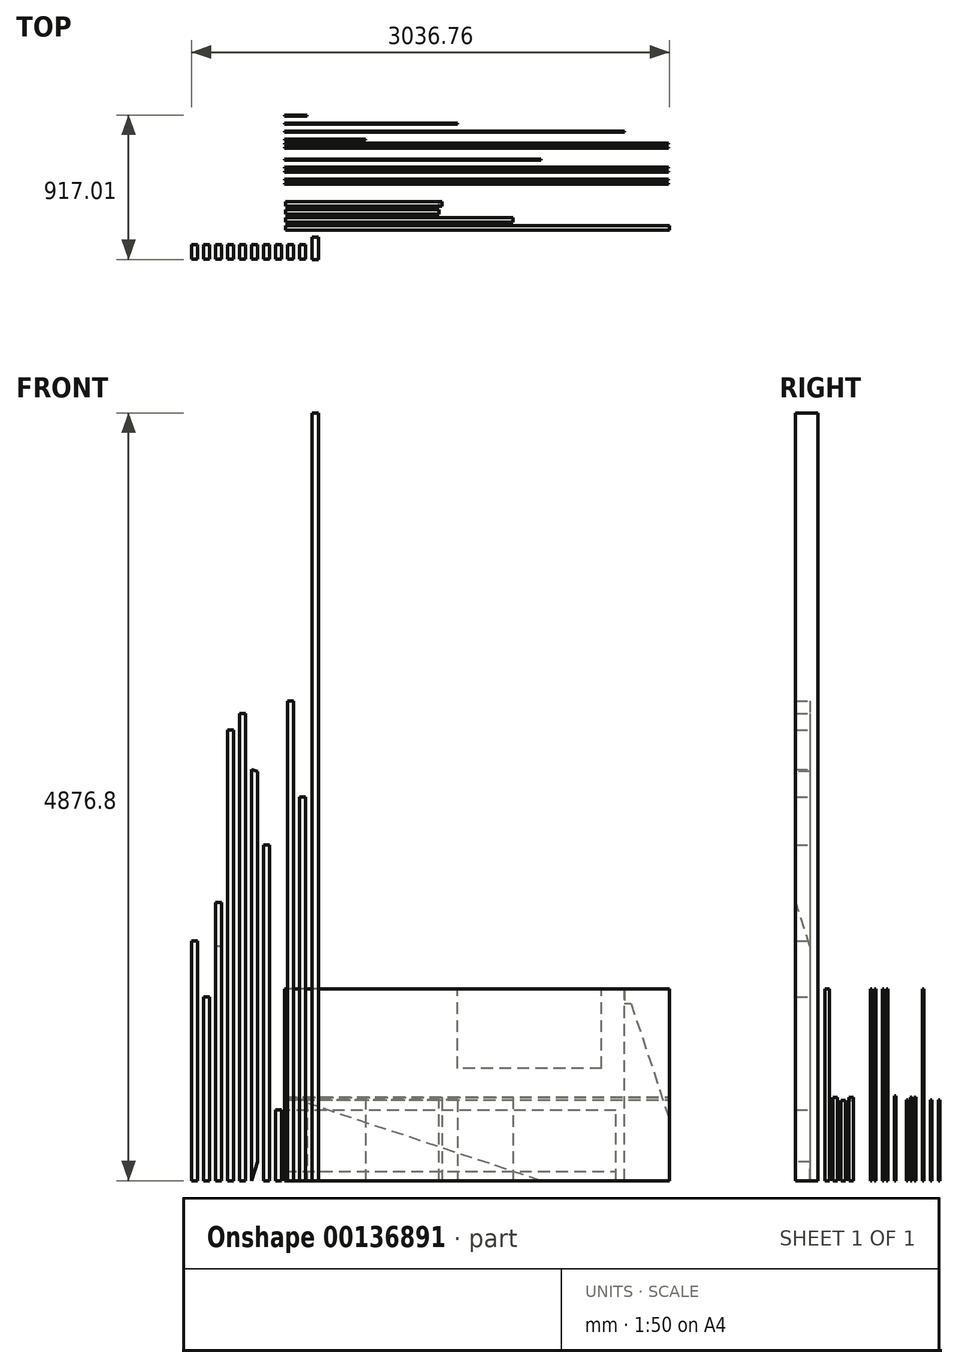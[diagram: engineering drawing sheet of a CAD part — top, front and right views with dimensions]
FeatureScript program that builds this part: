
annotation { "Feature Type Name" : "Feature", "Feature Type Description" : "" }
export const myFeature = defineFeature(function(context is Context, id is Id, definition is map)
    precondition{}
    {
        {
            var Q0;
            Q0=qCreatedBy(makeId("Top.planeOp"),FACE);
            var sketch = newSketch(context, id + "F0", { "sketchPlane" : qUnion([Q0])});
            skLineSegment(sketch, "E0.bottom", {"start": v(12.85, 155.38) * mm, "end": v(52.54, 155.38) * mm});
            skLineSegment(sketch, "E0.top", {"start": v(12.85, 12.5) * mm, "end": v(52.54, 12.5) * mm});
            skLineSegment(sketch, "E0.left", {"start": v(12.85, 155.38) * mm, "end": v(12.85, 12.5) * mm});
            skLineSegment(sketch, "E0.right", {"start": v(52.54, 155.38) * mm, "end": v(52.54, 12.5) * mm});
            skSolve(sketch);
        }
        {
            var Q0;
            Q0=makeQuery(id+"F0.imprint","IMPRINT",FACE,{"disambiguationData":[TD([[makeQuery(id+"F0.imprint","IMPRINT",EDGE,{"derivedFrom":sQuery(id+"F0.wireOp",EDGE,"E0.bottom")}),-1.0]])]});
            extrude(context, id + "F1", {"entities" : qUnion([Q0]), "depth" : 4876.8 * mm});
        }
        {
            var Q0;
            Q0=qCreatedBy(makeId("Top.planeOp"),FACE);
            var sketch = newSketch(context, id + "F2", { "sketchPlane" : qUnion([Q0])});
            skLineSegment(sketch, "E1.bottom", {"start": v(-27.7, 13.32) * mm, "end": v(-67.4, 13.32) * mm});
            skLineSegment(sketch, "E1.top", {"start": v(-27.7, 105.4) * mm, "end": v(-67.4, 105.4) * mm});
            skLineSegment(sketch, "E1.left", {"start": v(-27.7, 13.32) * mm, "end": v(-27.7, 105.4) * mm});
            skLineSegment(sketch, "E1.right", {"start": v(-67.4, 13.32) * mm, "end": v(-67.4, 105.4) * mm});
            skSolve(sketch);
        }
        {
            var Q0;
            Q0=makeQuery(id+"F2.imprint","IMPRINT",FACE,{"disambiguationData":[TD([[makeQuery(id+"F2.imprint","IMPRINT",EDGE,{"derivedFrom":sQuery(id+"F2.wireOp",EDGE,"E1.bottom")}),-1.0]])]});
            extrude(context, id + "F3", {"entities" : qUnion([Q0]), "depth" : 2438.4 * mm});
        }
        {
            var Q0;
            Q0=makeQuery(id+"F3.opExtrude","SWEPT_BODY",BODY,{"disambiguationData":[OSD([sQuery(id+"F2.wireOp",EDGE,"E1.bottom"),sQuery(id+"F2.wireOp",EDGE,"E1.top"),sQuery(id+"F2.wireOp",EDGE,"E1.left"),sQuery(id+"F2.wireOp",EDGE,"E1.right")])]});
            transform(context, id + "F4", {"entities" : qUnion([Q0]), "transformType" : TransformType.TRANSLATION_3D, "dx" : -76.2 * mm, "dy" : 0 * mm, "dz" : 0 * mm, "makeCopy" : true});
        }
        {
            var Q0;
            Q0=makeQuery(id+"F4.opPattern","COPY",FACE,{"derivedFrom":makeQuery(id+"F3.opExtrude","CAP_FACE",FACE,{"disambiguationData":[OSD([sQuery(id+"F2.wireOp",EDGE,"E1.bottom"),sQuery(id+"F2.wireOp",EDGE,"E1.top"),sQuery(id+"F2.wireOp",EDGE,"E1.left"),sQuery(id+"F2.wireOp",EDGE,"E1.right")])],"isStart":false}),"instanceName":"1"});
            extrude(context, id + "F5", {"entities" : qUnion([Q0]), "operationType" : NewBodyOperationType.ADD, "depth" : 609.6 * mm});
        }
        {
            var Q0;
            Q0=qCreatedBy(makeId("Top.planeOp"),FACE);
            var sketch = newSketch(context, id + "F6", { "sketchPlane" : qUnion([Q0])});
            skLineSegment(sketch, "E2.bottom", {"start": v(2283.56, 226) * mm, "end": v(-154.84, 226) * mm});
            skLineSegment(sketch, "E2.top", {"start": v(2283.56, 198.29) * mm, "end": v(-154.84, 198.29) * mm});
            skLineSegment(sketch, "E2.left", {"start": v(2283.56, 226) * mm, "end": v(2283.56, 198.29) * mm});
            skLineSegment(sketch, "E2.right", {"start": v(-154.84, 226) * mm, "end": v(-154.84, 198.29) * mm});
            skSolve(sketch);
        }
        {
            var Q0;
            Q0=makeQuery(id+"F6.imprint","IMPRINT",FACE,{"disambiguationData":[TD([[makeQuery(id+"F6.imprint","IMPRINT",EDGE,{"derivedFrom":sQuery(id+"F6.wireOp",EDGE,"E2.bottom")}),1.0]])]});
            extrude(context, id + "F7", {"entities" : qUnion([Q0]), "depth" : 1219.2 * mm});
        }
        {
            var Q0;
            Q0=makeQuery(id+"F3.opExtrude","SWEPT_BODY",BODY,{"disambiguationData":[OSD([sQuery(id+"F2.wireOp",EDGE,"E1.bottom"),sQuery(id+"F2.wireOp",EDGE,"E1.top"),sQuery(id+"F2.wireOp",EDGE,"E1.left"),sQuery(id+"F2.wireOp",EDGE,"E1.right")])]});
            transform(context, id + "F8", {"entities" : qUnion([Q0]), "transformType" : TransformType.TRANSLATION_3D, "dx" : -152.4 * mm, "dy" : 0 * mm, "dz" : 0 * mm, "makeCopy" : true});
        }
        {
            var Q0;
            Q0=makeQuery(id+"F8.opPattern","COPY",FACE,{"derivedFrom":makeQuery(id+"F3.opExtrude","CAP_FACE",FACE,{"disambiguationData":[OSD([sQuery(id+"F2.wireOp",EDGE,"E1.bottom"),sQuery(id+"F2.wireOp",EDGE,"E1.top"),sQuery(id+"F2.wireOp",EDGE,"E1.left"),sQuery(id+"F2.wireOp",EDGE,"E1.right")])],"isStart":false}),"instanceName":"1"});
            extrude(context, id + "F9", {"entities" : qUnion([Q0]), "operationType" : NewBodyOperationType.REMOVE, "oppositeDirection" : true, "depth" : 1987.55 * mm});
        }
        {
            var Q0;
            Q0=qCreatedBy(makeId("Top.planeOp"),FACE);
            var sketch = newSketch(context, id + "F10", { "sketchPlane" : qUnion([Q0])});
            skLineSegment(sketch, "E3.bottom", {"start": v(-155.66, 249.92) * mm, "end": v(1288.96, 249.92) * mm});
            skLineSegment(sketch, "E3.top", {"start": v(-155.66, 277.63) * mm, "end": v(1288.96, 277.63) * mm});
            skLineSegment(sketch, "E3.left", {"start": v(-155.66, 249.92) * mm, "end": v(-155.66, 277.63) * mm});
            skLineSegment(sketch, "E3.right", {"start": v(1288.96, 249.92) * mm, "end": v(1288.96, 277.63) * mm});
            skSolve(sketch);
        }
        {
            var Q0;
            Q0=makeQuery(id+"F10.imprint","IMPRINT",FACE,{"disambiguationData":[TD([[makeQuery(id+"F10.imprint","IMPRINT",EDGE,{"derivedFrom":sQuery(id+"F10.wireOp",EDGE,"E3.bottom")}),1.0]])]});
            extrude(context, id + "F11", {"entities" : qUnion([Q0]), "depth" : 530.23 * mm});
        }
        {
            var Q0;
            Q0=makeQuery(id+"F11.opExtrude","SWEPT_BODY",BODY,{"disambiguationData":[OSD([sQuery(id+"F10.wireOp",EDGE,"E3.bottom"),sQuery(id+"F10.wireOp",EDGE,"E3.top"),sQuery(id+"F10.wireOp",EDGE,"E3.left"),sQuery(id+"F10.wireOp",EDGE,"E3.right")])]});
            transform(context, id + "F12", {"entities" : qUnion([Q0]), "transformType" : TransformType.TRANSLATION_3D, "dx" : 0 * mm, "dy" : 50.8 * mm, "dz" : 0 * mm, "makeCopy" : true});
        }
        {
            var Q0;
            Q0=makeQuery(id+"F12.opPattern","COPY",FACE,{"derivedFrom":makeQuery(id+"F11.opExtrude","SWEPT_FACE",FACE,{"disambiguationData":[OSD([sQuery(id+"F10.wireOp",EDGE,"E3.right")])]}),"instanceName":"1"});
            extrude(context, id + "F13", {"entities" : qUnion([Q0]), "operationType" : NewBodyOperationType.REMOVE, "oppositeDirection" : true, "depth" : 450.85 * mm});
        }
        {
            var Q0;
            Q0=makeQuery(id+"F3.opExtrude","SWEPT_BODY",BODY,{"disambiguationData":[OSD([sQuery(id+"F2.wireOp",EDGE,"E1.bottom"),sQuery(id+"F2.wireOp",EDGE,"E1.top"),sQuery(id+"F2.wireOp",EDGE,"E1.left"),sQuery(id+"F2.wireOp",EDGE,"E1.right")])]});
            transform(context, id + "F14", {"entities" : qUnion([Q0]), "transformType" : TransformType.TRANSLATION_3D, "dx" : -228.6 * mm, "dy" : 0 * mm, "dz" : 0 * mm, "makeCopy" : true});
        }
        {
            var Q0;
            Q0=makeQuery(id+"F14.opPattern","COPY",FACE,{"derivedFrom":makeQuery(id+"F3.opExtrude","CAP_FACE",FACE,{"disambiguationData":[OSD([sQuery(id+"F2.wireOp",EDGE,"E1.bottom"),sQuery(id+"F2.wireOp",EDGE,"E1.top"),sQuery(id+"F2.wireOp",EDGE,"E1.left"),sQuery(id+"F2.wireOp",EDGE,"E1.right")])],"isStart":false}),"instanceName":"1"});
            extrude(context, id + "F15", {"entities" : qUnion([Q0]), "operationType" : NewBodyOperationType.REMOVE, "oppositeDirection" : true, "depth" : 304.8 * mm});
        }
        {
            var Q0;
            Q0=makeQuery(id+"F3.opExtrude","SWEPT_BODY",BODY,{"disambiguationData":[OSD([sQuery(id+"F2.wireOp",EDGE,"E1.bottom"),sQuery(id+"F2.wireOp",EDGE,"E1.top"),sQuery(id+"F2.wireOp",EDGE,"E1.left"),sQuery(id+"F2.wireOp",EDGE,"E1.right")])]});
            transform(context, id + "F16", {"entities" : qUnion([Q0]), "transformType" : TransformType.TRANSLATION_3D, "dx" : -457.2 * mm, "dy" : 0 * mm, "dz" : 0 * mm, "makeCopy" : true});
        }
        {
            var Q0;
            Q0=makeQuery(id+"F16.opPattern","COPY",FACE,{"derivedFrom":makeQuery(id+"F3.opExtrude","CAP_FACE",FACE,{"disambiguationData":[OSD([sQuery(id+"F2.wireOp",EDGE,"E1.bottom"),sQuery(id+"F2.wireOp",EDGE,"E1.top"),sQuery(id+"F2.wireOp",EDGE,"E1.left"),sQuery(id+"F2.wireOp",EDGE,"E1.right")])],"isStart":false}),"instanceName":"1"});
            extrude(context, id + "F17", {"entities" : qUnion([Q0]), "operationType" : NewBodyOperationType.ADD, "depth" : 425.45 * mm});
        }
        {
            var Q0;
            Q0=makeQuery(id+"F3.opExtrude","SWEPT_BODY",BODY,{"disambiguationData":[OSD([sQuery(id+"F2.wireOp",EDGE,"E1.bottom"),sQuery(id+"F2.wireOp",EDGE,"E1.top"),sQuery(id+"F2.wireOp",EDGE,"E1.left"),sQuery(id+"F2.wireOp",EDGE,"E1.right")])]});
            transform(context, id + "F18", {"entities" : qUnion([Q0]), "transformType" : TransformType.TRANSLATION_3D, "dx" : -304.8 * mm, "dy" : 0 * mm, "dz" : 0 * mm, "makeCopy" : true});
        }
        {
            var Q0;
            Q0=makeQuery(id+"F18.opPattern","COPY",FACE,{"derivedFrom":makeQuery(id+"F3.opExtrude","CAP_FACE",FACE,{"disambiguationData":[OSD([sQuery(id+"F2.wireOp",EDGE,"E1.bottom"),sQuery(id+"F2.wireOp",EDGE,"E1.top"),sQuery(id+"F2.wireOp",EDGE,"E1.left"),sQuery(id+"F2.wireOp",EDGE,"E1.right")])],"isStart":false}),"instanceName":"1"});
            extrude(context, id + "F19", {"entities" : qUnion([Q0]), "operationType" : NewBodyOperationType.ADD, "depth" : 172.56 * mm});
        }
        {
            var Q0;
            {var subQ0=sQuery(id+"F2.wireOp",EDGE,"E1.bottom");Q0=makeQuery(id+"F19.boolean.opBoolean","MERGE",FACE,{"derivedFrom":[makeQuery(id+"F18.opPattern","COPY",FACE,{"derivedFrom":makeQuery(id+"F3.opExtrude","SWEPT_FACE",FACE,{"disambiguationData":[OSD([subQ0])]}),"instanceName":"1"}),makeQuery(id+"F19.opExtrude","SWEPT_FACE",FACE,{"disambiguationData":[OSD([subQ0])]})]});}
            var sketch = newSketch(context, id + "F20", { "sketchPlane" : qUnion([Q0])});
            skLineSegment(sketch, "E4", {"start": v(-372.2, 2610.96) * mm, "end": v(-332.5, 2597.8) * mm});
            skLineSegment(sketch, "E5", {"start": v(-372.2, 0) * mm, "end": v(-332.5, 119.6) * mm});
            skSolve(sketch);
        }
        {
            var Q0;
            {var subQ0=sQuery(id+"F20.wireOp",EDGE,"E5");Q0=makeQuery(id+"F20.imprint","IMPRINT",FACE,{"disambiguationData":[TD([[makeQuery(id+"F20.imprint","IMPRINT",EDGE,{"derivedFrom":subQ0}),-1.0]])]});}
            var Q1;
            {var subQ0=sQuery(id+"F20.wireOp",EDGE,"E4");Q1=makeQuery(id+"F20.imprint","IMPRINT",FACE,{"disambiguationData":[TD([[makeQuery(id+"F20.imprint","IMPRINT",EDGE,{"derivedFrom":subQ0}),1.0]])]});}
            extrude(context, id + "F21", {"entities" : qUnion([Q0, Q1]), "operationType" : NewBodyOperationType.REMOVE, "oppositeDirection" : true, "depth" : 152.4 * mm});
        }
        {
            var Q0;
            Q0=makeQuery(id+"F3.opExtrude","SWEPT_BODY",BODY,{"disambiguationData":[OSD([sQuery(id+"F2.wireOp",EDGE,"E1.bottom"),sQuery(id+"F2.wireOp",EDGE,"E1.top"),sQuery(id+"F2.wireOp",EDGE,"E1.left"),sQuery(id+"F2.wireOp",EDGE,"E1.right")])]});
            transform(context, id + "F22", {"entities" : qUnion([Q0]), "transformType" : TransformType.TRANSLATION_3D, "dx" : -381 * mm, "dy" : 0 * mm, "dz" : 0 * mm, "makeCopy" : true});
        }
        {
            var Q0;
            Q0=makeQuery(id+"F22.opPattern","COPY",FACE,{"derivedFrom":makeQuery(id+"F3.opExtrude","CAP_FACE",FACE,{"disambiguationData":[OSD([sQuery(id+"F2.wireOp",EDGE,"E1.bottom"),sQuery(id+"F2.wireOp",EDGE,"E1.top"),sQuery(id+"F2.wireOp",EDGE,"E1.left"),sQuery(id+"F2.wireOp",EDGE,"E1.right")])],"isStart":false}),"instanceName":"1"});
            extrude(context, id + "F23", {"entities" : qUnion([Q0]), "operationType" : NewBodyOperationType.ADD, "depth" : 530.23 * mm});
        }
        {
            var Q0;
            Q0=qCreatedBy(makeId("Top.planeOp"),FACE);
            var sketch = newSketch(context, id + "F24", { "sketchPlane" : qUnion([Q0])});
            skLineSegment(sketch, "E6.bottom", {"start": v(-162.06, 488.98) * mm, "end": v(2276.34, 488.98) * mm});
            skLineSegment(sketch, "E6.top", {"start": v(-162.06, 497.72) * mm, "end": v(2276.34, 497.72) * mm});
            skLineSegment(sketch, "E6.left", {"start": v(-162.06, 488.98) * mm, "end": v(-162.06, 497.72) * mm});
            skLineSegment(sketch, "E6.right", {"start": v(2276.34, 488.98) * mm, "end": v(2276.34, 497.72) * mm});
            skSolve(sketch);
        }
        {
            var Q0;
            Q0=makeQuery(id+"F24.imprint","IMPRINT",FACE,{"disambiguationData":[TD([[makeQuery(id+"F24.imprint","IMPRINT",EDGE,{"derivedFrom":sQuery(id+"F24.wireOp",EDGE,"E6.bottom")}),1.0]])]});
            extrude(context, id + "F25", {"entities" : qUnion([Q0]), "depth" : 1219.2 * mm});
        }
        {
            var Q0;
            Q0=makeQuery(id+"F12.opPattern","COPY",FACE,{"derivedFrom":makeQuery(id+"F11.opExtrude","SWEPT_FACE",FACE,{"disambiguationData":[OSD([sQuery(id+"F10.wireOp",EDGE,"E3.top")])]}),"instanceName":"1"});
            var sketch = newSketch(context, id + "F26", { "sketchPlane" : qUnion([Q0])});
            skLineSegment(sketch, "E7", {"start": v(-818.27, 0) * mm, "end": v(-818.27, 510.38) * mm});
            skLineSegment(sketch, "E8", {"start": v(-818.27, 510.38) * mm, "end": v(155.66, 510.38) * mm});
            skSolve(sketch);
        }
        {
            var Q0;
            Q0=makeQuery(id+"F12.opPattern","COPY",BODY,{"derivedFrom":makeQuery(id+"F11.opExtrude","SWEPT_BODY",BODY,{"disambiguationData":[OSD([sQuery(id+"F10.wireOp",EDGE,"E3.bottom"),sQuery(id+"F10.wireOp",EDGE,"E3.top"),sQuery(id+"F10.wireOp",EDGE,"E3.left"),sQuery(id+"F10.wireOp",EDGE,"E3.right")])]}),"instanceName":"1"});
            transform(context, id + "F27", {"entities" : qUnion([Q0]), "transformType" : TransformType.TRANSLATION_3D, "dx" : 0 * mm, "dy" : 50.8 * mm, "dz" : 0 * mm, "makeCopy" : true});
        }
        {
            var Q0;
            Q0=makeQuery(id+"F27.opPattern","COPY",FACE,{"derivedFrom":makeQuery(id+"F12.opPattern","COPY",FACE,{"derivedFrom":makeQuery(id+"F11.opExtrude","SWEPT_FACE",FACE,{"disambiguationData":[OSD([sQuery(id+"F10.wireOp",EDGE,"E3.top")])]}),"instanceName":"1"}),"instanceName":"1"});
            var sketch = newSketch(context, id + "F28", { "sketchPlane" : qUnion([Q0])});
            skLineSegment(sketch, "E9", {"start": v(-818.27, 0) * mm, "end": v(-818.27, 510.38) * mm});
            skLineSegment(sketch, "E10", {"start": v(-818.27, 510.38) * mm, "end": v(155.66, 510.38) * mm});
            skSolve(sketch);
        }
        {
            var Q0;
            {var subQ4=sQuery(id+"F26.wireOp",EDGE,"E7");Q0=makeQuery(id+"F26.imprint","IMPRINT",FACE,{"disambiguationData":[TD([[makeQuery(id+"F26.imprint","IMPRINT",EDGE,{"derivedFrom":subQ4}),1.0]])]});}
            extrude(context, id + "F29", {"entities" : qUnion([Q0]), "operationType" : NewBodyOperationType.REMOVE, "oppositeDirection" : true, "depth" : 50.8 * mm});
        }
        {
            var Q0;
            {var subQ0=sQuery(id+"F28.wireOp",EDGE,"E9");Q0=makeQuery(id+"F28.imprint","IMPRINT",FACE,{"disambiguationData":[TD([[makeQuery(id+"F28.imprint","IMPRINT",EDGE,{"derivedFrom":subQ0}),-1.0]])]});}
            extrude(context, id + "F30", {"entities" : qUnion([Q0]), "operationType" : NewBodyOperationType.REMOVE, "oppositeDirection" : true, "depth" : 50.8 * mm});
        }
        {
            var Q0;
            Q0=makeQuery(id+"F25.opExtrude","SWEPT_BODY",BODY,{"disambiguationData":[OSD([sQuery(id+"F24.wireOp",EDGE,"E6.bottom"),sQuery(id+"F24.wireOp",EDGE,"E6.top"),sQuery(id+"F24.wireOp",EDGE,"E6.left"),sQuery(id+"F24.wireOp",EDGE,"E6.right")])]});
            transform(context, id + "F31", {"entities" : qUnion([Q0]), "transformType" : TransformType.TRANSLATION_3D, "dx" : 0 * mm, "dy" : 76.2 * mm, "dz" : 0 * mm, "makeCopy" : true});
        }
        {
            var Q0;
            Q0=makeQuery(id+"F31.opPattern","COPY",FACE,{"derivedFrom":makeQuery(id+"F25.opExtrude","SWEPT_FACE",FACE,{"disambiguationData":[OSD([sQuery(id+"F24.wireOp",EDGE,"E6.top")])]}),"instanceName":"1"});
            var sketch = newSketch(context, id + "F32", { "sketchPlane" : qUnion([Q0])});
            skLineSegment(sketch, "E11", {"start": v(-1996.21, 1219.2) * mm, "end": v(-1996.21, 1127.13) * mm});
            skLineSegment(sketch, "E12", {"start": v(-1996.21, 1127.13) * mm, "end": v(-2037.8, 1127.13) * mm});
            skLineSegment(sketch, "E13", {"start": v(-2037.8, 1127.13) * mm, "end": v(-2276.34, 408.4) * mm});
            skSolve(sketch);
        }
        {
            var Q0;
            {var subQ5=sQuery(id+"F32.wireOp",EDGE,"E11");Q0=makeQuery(id+"F32.imprint","IMPRINT",FACE,{"disambiguationData":[TD([[makeQuery(id+"F32.imprint","IMPRINT",EDGE,{"derivedFrom":subQ5}),-1.0]])]});}
            extrude(context, id + "F33", {"entities" : qUnion([Q0]), "operationType" : NewBodyOperationType.REMOVE, "oppositeDirection" : true, "depth" : 25.4 * mm});
        }
        {
            var Q0;
            Q0=makeQuery(id+"F25.opExtrude","SWEPT_BODY",BODY,{"disambiguationData":[OSD([sQuery(id+"F24.wireOp",EDGE,"E6.bottom"),sQuery(id+"F24.wireOp",EDGE,"E6.top"),sQuery(id+"F24.wireOp",EDGE,"E6.left"),sQuery(id+"F24.wireOp",EDGE,"E6.right")])]});
            transform(context, id + "F34", {"entities" : qUnion([Q0]), "transformType" : TransformType.TRANSLATION_3D, "dx" : 0 * mm, "dy" : 152.4 * mm, "dz" : 0 * mm, "makeCopy" : true});
        }
        {
            var Q0;
            Q0=makeQuery(id+"F34.opPattern","COPY",FACE,{"derivedFrom":makeQuery(id+"F25.opExtrude","SWEPT_FACE",FACE,{"disambiguationData":[OSD([sQuery(id+"F24.wireOp",EDGE,"E6.top")])]}),"instanceName":"1"});
            var sketch = newSketch(context, id + "F35", { "sketchPlane" : qUnion([Q0])});
            skLineSegment(sketch, "E14", {"start": v(-1465.54, 0) * mm, "end": v(162.06, 540.07) * mm});
            skSolve(sketch);
        }
        {
            var Q0;
            {var subQ3=sQuery(id+"F35.wireOp",EDGE,"E14");Q0=makeQuery(id+"F35.imprint","IMPRINT",FACE,{"disambiguationData":[TD([[makeQuery(id+"F35.imprint","IMPRINT",EDGE,{"derivedFrom":subQ3}),1.0]])]});}
            extrude(context, id + "F36", {"entities" : qUnion([Q0]), "operationType" : NewBodyOperationType.REMOVE, "oppositeDirection" : true, "depth" : 25.4 * mm});
        }
        {
            var Q0;
            Q0=makeQuery(id+"F25.opExtrude","SWEPT_BODY",BODY,{"disambiguationData":[OSD([sQuery(id+"F24.wireOp",EDGE,"E6.bottom"),sQuery(id+"F24.wireOp",EDGE,"E6.top"),sQuery(id+"F24.wireOp",EDGE,"E6.left"),sQuery(id+"F24.wireOp",EDGE,"E6.right")])]});
            transform(context, id + "F37", {"entities" : qUnion([Q0]), "transformType" : TransformType.TRANSLATION_3D, "dx" : 0 * mm, "dy" : 228.6 * mm, "dz" : 0 * mm, "makeCopy" : true});
        }
        {
            var Q0;
            Q0=makeQuery(id+"F37.opPattern","COPY",FACE,{"derivedFrom":makeQuery(id+"F25.opExtrude","CAP_FACE",FACE,{"disambiguationData":[OSD([sQuery(id+"F24.wireOp",EDGE,"E6.bottom"),sQuery(id+"F24.wireOp",EDGE,"E6.top"),sQuery(id+"F24.wireOp",EDGE,"E6.left"),sQuery(id+"F24.wireOp",EDGE,"E6.right")])],"isStart":false}),"instanceName":"1"});
            extrude(context, id + "F38", {"entities" : qUnion([Q0]), "operationType" : NewBodyOperationType.REMOVE, "oppositeDirection" : true, "depth" : 706.45 * mm});
        }
        {
            var Q0;
            Q0=makeQuery(id+"F31.opPattern","COPY",BODY,{"derivedFrom":makeQuery(id+"F25.opExtrude","SWEPT_BODY",BODY,{"disambiguationData":[OSD([sQuery(id+"F24.wireOp",EDGE,"E6.bottom"),sQuery(id+"F24.wireOp",EDGE,"E6.top"),sQuery(id+"F24.wireOp",EDGE,"E6.left"),sQuery(id+"F24.wireOp",EDGE,"E6.right")])]}),"instanceName":"1"});
            transform(context, id + "F39", {"entities" : qUnion([Q0]), "transformType" : TransformType.TRANSLATION_3D, "dx" : 0 * mm, "dy" : 25.4 * mm, "dz" : 0 * mm, "makeCopy" : true});
        }
        {
            var Q0;
            Q0=makeQuery(id+"F39.opPattern","COPY",FACE,{"derivedFrom":makeQuery(id+"F31.opPattern","COPY",FACE,{"derivedFrom":makeQuery(id+"F25.opExtrude","SWEPT_FACE",FACE,{"disambiguationData":[OSD([sQuery(id+"F24.wireOp",EDGE,"E6.top")])]}),"instanceName":"1"}),"instanceName":"1"});
            var sketch = newSketch(context, id + "F40", { "sketchPlane" : qUnion([Q0])});
            skLineSegment(sketch, "E15", {"start": v(162.06, 60.33) * mm, "end": v(-1943.82, 60.32) * mm});
            skLineSegment(sketch, "E16", {"start": v(-1943.82, 0) * mm, "end": v(-1943.82, 60.32) * mm});
            skSolve(sketch);
        }
        {
            var Q0;
            {var subQ0=sQuery(id+"F40.wireOp",EDGE,"E15");Q0=makeQuery(id+"F40.imprint","IMPRINT",FACE,{"disambiguationData":[TD([[makeQuery(id+"F40.imprint","IMPRINT",EDGE,{"derivedFrom":subQ0}),1.0]])]});}
            extrude(context, id + "F41", {"entities" : qUnion([Q0]), "operationType" : NewBodyOperationType.REMOVE, "oppositeDirection" : true, "depth" : 25.4 * mm});
        }
        {
            var Q0;
            Q0=makeQuery(id+"F25.opExtrude","SWEPT_BODY",BODY,{"disambiguationData":[OSD([sQuery(id+"F24.wireOp",EDGE,"E6.bottom"),sQuery(id+"F24.wireOp",EDGE,"E6.top"),sQuery(id+"F24.wireOp",EDGE,"E6.left"),sQuery(id+"F24.wireOp",EDGE,"E6.right")])]});
            transform(context, id + "F42", {"entities" : qUnion([Q0]), "transformType" : TransformType.TRANSLATION_3D, "dx" : 0 * mm, "dy" : 25.4 * mm, "dz" : 0 * mm, "makeCopy" : true});
        }
        {
            var Q0;
            Q0=makeQuery(id+"F42.opPattern","COPY",FACE,{"derivedFrom":makeQuery(id+"F25.opExtrude","SWEPT_FACE",FACE,{"disambiguationData":[OSD([sQuery(id+"F24.wireOp",EDGE,"E6.top")])]}),"instanceName":"1"});
            var sketch = newSketch(context, id + "F43", { "sketchPlane" : qUnion([Q0])});
            skLineSegment(sketch, "E17", {"start": v(-1943.82, 0) * mm, "end": v(-1943.82, 447.68) * mm});
            skLineSegment(sketch, "E18", {"start": v(-1943.82, 447.67) * mm, "end": v(162.06, 447.68) * mm});
            skSolve(sketch);
        }
        {
            var Q0;
            {var subQ0=sQuery(id+"F43.wireOp",EDGE,"E17");Q0=makeQuery(id+"F43.imprint","IMPRINT",FACE,{"disambiguationData":[TD([[makeQuery(id+"F43.imprint","IMPRINT",EDGE,{"derivedFrom":subQ0}),-1.0]])]});}
            extrude(context, id + "F44", {"entities" : qUnion([Q0]), "operationType" : NewBodyOperationType.REMOVE, "oppositeDirection" : true, "depth" : 25.4 * mm});
        }
        {
            var Q0;
            Q0=makeQuery(id+"F37.opPattern","COPY",BODY,{"derivedFrom":makeQuery(id+"F25.opExtrude","SWEPT_BODY",BODY,{"disambiguationData":[OSD([sQuery(id+"F24.wireOp",EDGE,"E6.bottom"),sQuery(id+"F24.wireOp",EDGE,"E6.top"),sQuery(id+"F24.wireOp",EDGE,"E6.left"),sQuery(id+"F24.wireOp",EDGE,"E6.right")])]}),"instanceName":"1"});
            transform(context, id + "F45", {"entities" : qUnion([Q0]), "transformType" : TransformType.TRANSLATION_3D, "dx" : 0 * mm, "dy" : 25.4 * mm, "dz" : 0 * mm, "makeCopy" : true});
        }
        {
            var Q0;
            Q0=makeQuery(id+"F45.opPattern","COPY",FACE,{"derivedFrom":makeQuery(id+"F38.boolean.opBoolean","COPY",FACE,{"derivedFrom":makeQuery(id+"F38.opExtrude","CAP_FACE",FACE,{"disambiguationData":[OSD([sQuery(id+"F24.wireOp",EDGE,"E6.bottom"),sQuery(id+"F24.wireOp",EDGE,"E6.top"),sQuery(id+"F24.wireOp",EDGE,"E6.left"),sQuery(id+"F24.wireOp",EDGE,"E6.right")])],"isStart":false})}),"instanceName":"1"});
            extrude(context, id + "F46", {"entities" : qUnion([Q0]), "operationType" : NewBodyOperationType.ADD, "depth" : 27.32 * mm});
        }
        {
            var Q0;
            {var subQ0=sQuery(id+"F24.wireOp",EDGE,"E6.right");Q0=makeQuery(id+"F46.boolean.opBoolean","MERGE",FACE,{"derivedFrom":[makeQuery(id+"F45.opPattern","COPY",FACE,{"derivedFrom":makeQuery(id+"F37.opPattern","COPY",FACE,{"derivedFrom":makeQuery(id+"F25.opExtrude","SWEPT_FACE",FACE,{"disambiguationData":[OSD([subQ0])]}),"instanceName":"1"}),"instanceName":"1"}),makeQuery(id+"F46.opExtrude","SWEPT_FACE",FACE,{"disambiguationData":[OSD([subQ0])]})]});}
            var sketch = newSketch(context, id + "F47", { "sketchPlane" : qUnion([Q0])});
            skLineSegment(sketch, "E19", {"start": v(751.72, 540.07) * mm, "end": v(742.98, 537.17) * mm});
            skLineSegment(sketch, "E20", {"start": v(751.72, 531.33) * mm, "end": v(742.98, 528.44) * mm});
            skSolve(sketch);
        }
        {
            var Q0;
            {var subQ0=sQuery(id+"F47.wireOp",EDGE,"E19");Q0=makeQuery(id+"F47.imprint","IMPRINT",FACE,{"disambiguationData":[TD([[makeQuery(id+"F47.imprint","IMPRINT",EDGE,{"derivedFrom":subQ0}),-1.0]])]});}
            var Q1;
            {var subQ0=sQuery(id+"F47.wireOp",EDGE,"E19");Q1=makeQuery(id+"F47.imprint","IMPRINT",FACE,{"disambiguationData":[TD([[makeQuery(id+"F47.imprint","IMPRINT",EDGE,{"derivedFrom":subQ0}),1.0]])]});}
            extrude(context, id + "F48", {"entities" : qUnion([Q0, Q1]), "operationType" : NewBodyOperationType.REMOVE, "oppositeDirection" : true, "depth" : 2540 * mm});
        }
        {
            var Q0;
            Q0=makeQuery(id+"F45.opPattern","COPY",BODY,{"derivedFrom":makeQuery(id+"F37.opPattern","COPY",BODY,{"derivedFrom":makeQuery(id+"F25.opExtrude","SWEPT_BODY",BODY,{"disambiguationData":[OSD([sQuery(id+"F24.wireOp",EDGE,"E6.bottom"),sQuery(id+"F24.wireOp",EDGE,"E6.top"),sQuery(id+"F24.wireOp",EDGE,"E6.left"),sQuery(id+"F24.wireOp",EDGE,"E6.right")])]}),"instanceName":"1"}),"instanceName":"1"});
            transform(context, id + "F49", {"entities" : qUnion([Q0]), "transformType" : TransformType.TRANSLATION_3D, "dx" : 0 * mm, "dy" : 25.4 * mm, "dz" : 0 * mm, "makeCopy" : true});
        }
        {
            var Q0;
            {var subQ0=sQuery(id+"F24.wireOp",EDGE,"E6.right");Q0=makeQuery(id+"F49.opPattern","COPY",FACE,{"derivedFrom":makeQuery(id+"F46.boolean.opBoolean","MERGE",FACE,{"derivedFrom":[makeQuery(id+"F45.opPattern","COPY",FACE,{"derivedFrom":makeQuery(id+"F37.opPattern","COPY",FACE,{"derivedFrom":makeQuery(id+"F25.opExtrude","SWEPT_FACE",FACE,{"disambiguationData":[OSD([subQ0])]}),"instanceName":"1"}),"instanceName":"1"}),makeQuery(id+"F46.opExtrude","SWEPT_FACE",FACE,{"disambiguationData":[OSD([subQ0])]})]}),"instanceName":"1"});}
            extrude(context, id + "F50", {"entities" : qUnion([Q0]), "operationType" : NewBodyOperationType.REMOVE, "oppositeDirection" : true, "depth" : 1925.65 * mm});
        }
        {
            var Q0;
            Q0=makeQuery(id+"F3.opExtrude","SWEPT_BODY",BODY,{"disambiguationData":[OSD([sQuery(id+"F2.wireOp",EDGE,"E1.bottom"),sQuery(id+"F2.wireOp",EDGE,"E1.top"),sQuery(id+"F2.wireOp",EDGE,"E1.left"),sQuery(id+"F2.wireOp",EDGE,"E1.right")])]});
            transform(context, id + "F51", {"entities" : qUnion([Q0]), "transformType" : TransformType.TRANSLATION_3D, "dx" : -533.4 * mm, "dy" : 0 * mm, "dz" : 0 * mm, "makeCopy" : true});
        }
        {
            var Q0;
            Q0=makeQuery(id+"F51.opPattern","COPY",FACE,{"derivedFrom":makeQuery(id+"F3.opExtrude","SWEPT_FACE",FACE,{"disambiguationData":[OSD([sQuery(id+"F2.wireOp",EDGE,"E1.right")])]}),"instanceName":"1"});
            var sketch = newSketch(context, id + "F52", { "sketchPlane" : qUnion([Q0])});
            skLineSegment(sketch, "E21", {"start": v(-59.35, 0) * mm, "end": v(-59.35, 1627.6) * mm});
            skLineSegment(sketch, "E22", {"start": v(-105.4, 1488.9) * mm, "end": v(-59.35, 1627.6) * mm});
            skLineSegment(sketch, "E23", {"start": v(-59.35, 1627.6) * mm, "end": v(-13.32, 1766.33) * mm});
            skSolve(sketch);
        }
        {
            var Q0;
            {var subQ4=sQuery(id+"F52.wireOp",EDGE,"E22");Q0=makeQuery(id+"F52.imprint","IMPRINT",FACE,{"disambiguationData":[TD([[makeQuery(id+"F52.imprint","IMPRINT",EDGE,{"derivedFrom":subQ4}),1.0]])]});}
            extrude(context, id + "F53", {"entities" : qUnion([Q0]), "operationType" : NewBodyOperationType.REMOVE, "oppositeDirection" : true, "depth" : 50.8 * mm});
        }
        {
            var Q0;
            Q0=makeQuery(id+"F3.opExtrude","SWEPT_BODY",BODY,{"disambiguationData":[OSD([sQuery(id+"F2.wireOp",EDGE,"E1.bottom"),sQuery(id+"F2.wireOp",EDGE,"E1.top"),sQuery(id+"F2.wireOp",EDGE,"E1.left"),sQuery(id+"F2.wireOp",EDGE,"E1.right")])]});
            transform(context, id + "F54", {"entities" : qUnion([Q0]), "transformType" : TransformType.TRANSLATION_3D, "dx" : -609.6 * mm, "dy" : 0 * mm, "dz" : 0 * mm, "makeCopy" : true});
        }
        {
            var Q0;
            Q0=makeQuery(id+"F54.opPattern","COPY",FACE,{"derivedFrom":makeQuery(id+"F3.opExtrude","CAP_FACE",FACE,{"disambiguationData":[OSD([sQuery(id+"F2.wireOp",EDGE,"E1.bottom"),sQuery(id+"F2.wireOp",EDGE,"E1.top"),sQuery(id+"F2.wireOp",EDGE,"E1.left"),sQuery(id+"F2.wireOp",EDGE,"E1.right")])],"isStart":false}),"instanceName":"1"});
            extrude(context, id + "F55", {"entities" : qUnion([Q0]), "operationType" : NewBodyOperationType.REMOVE, "oppositeDirection" : true, "depth" : 1270 * mm});
        }
        {
            var Q0;
            Q0=makeQuery(id+"F3.opExtrude","SWEPT_BODY",BODY,{"disambiguationData":[OSD([sQuery(id+"F2.wireOp",EDGE,"E1.bottom"),sQuery(id+"F2.wireOp",EDGE,"E1.top"),sQuery(id+"F2.wireOp",EDGE,"E1.left"),sQuery(id+"F2.wireOp",EDGE,"E1.right")])]});
            transform(context, id + "F56", {"entities" : qUnion([Q0]), "transformType" : TransformType.TRANSLATION_3D, "dx" : -685.8 * mm, "dy" : 0 * mm, "dz" : 0 * mm, "makeCopy" : true});
        }
        {
            var Q0;
            Q0=makeQuery(id+"F56.opPattern","COPY",FACE,{"derivedFrom":makeQuery(id+"F3.opExtrude","CAP_FACE",FACE,{"disambiguationData":[OSD([sQuery(id+"F2.wireOp",EDGE,"E1.bottom"),sQuery(id+"F2.wireOp",EDGE,"E1.top"),sQuery(id+"F2.wireOp",EDGE,"E1.left"),sQuery(id+"F2.wireOp",EDGE,"E1.right")])],"isStart":false}),"instanceName":"1"});
            extrude(context, id + "F57", {"entities" : qUnion([Q0]), "operationType" : NewBodyOperationType.REMOVE, "oppositeDirection" : true, "depth" : 914.4 * mm});
        }
        {
            var Q0;
            Q0=makeQuery(id+"F25.opExtrude","SWEPT_BODY",BODY,{"disambiguationData":[OSD([sQuery(id+"F24.wireOp",EDGE,"E6.bottom"),sQuery(id+"F24.wireOp",EDGE,"E6.top"),sQuery(id+"F24.wireOp",EDGE,"E6.left"),sQuery(id+"F24.wireOp",EDGE,"E6.right")])]});
            transform(context, id + "F58", {"entities" : qUnion([Q0]), "transformType" : TransformType.TRANSLATION_3D, "dx" : 0 * mm, "dy" : 330.2 * mm, "dz" : 0 * mm, "makeCopy" : true});
        }
        {
            var Q0;
            Q0=makeQuery(id+"F58.opPattern","COPY",FACE,{"derivedFrom":makeQuery(id+"F25.opExtrude","SWEPT_FACE",FACE,{"disambiguationData":[OSD([sQuery(id+"F24.wireOp",EDGE,"E6.top")])]}),"instanceName":"1"});
            var sketch = newSketch(context, id + "F59", { "sketchPlane" : qUnion([Q0])});
            skLineSegment(sketch, "E24", {"start": v(-1996.21, 0) * mm, "end": v(-1996.21, 713.57) * mm});
            skLineSegment(sketch, "E25", {"start": v(-1996.21, 713.57) * mm, "end": v(162.06, 713.57) * mm});
            skLineSegment(sketch, "E26", {"start": v(-937.35, 713.57) * mm, "end": v(-937.35, 1219.2) * mm});
            skLineSegment(sketch, "E27.bottom", {"start": v(-1996.21, 713.57) * mm, "end": v(-1851.75, 713.57) * mm});
            skLineSegment(sketch, "E27.top", {"start": v(-1996.21, 1219.2) * mm, "end": v(-1851.75, 1219.2) * mm});
            skLineSegment(sketch, "E27.left", {"start": v(-1996.21, 713.57) * mm, "end": v(-1996.21, 1219.2) * mm});
            skLineSegment(sketch, "E27.right", {"start": v(-1851.75, 713.57) * mm, "end": v(-1851.75, 1219.2) * mm});
            skSolve(sketch);
        }
        {
            var Q0;
            {var subQ4=sQuery(id+"F59.wireOp",EDGE,"E24");Q0=makeQuery(id+"F59.imprint","IMPRINT",FACE,{"disambiguationData":[TD([[makeQuery(id+"F59.imprint","IMPRINT",EDGE,{"derivedFrom":subQ4}),1.0]])]});}
            var Q1;
            {var subQ2=sQuery(id+"F59.wireOp",EDGE,"E26");Q1=makeQuery(id+"F59.imprint","IMPRINT",FACE,{"disambiguationData":[TD([[makeQuery(id+"F59.imprint","IMPRINT",EDGE,{"derivedFrom":subQ2}),1.0]])]});}
            extrude(context, id + "F60", {"entities" : qUnion([Q0, Q1]), "operationType" : NewBodyOperationType.REMOVE, "oppositeDirection" : true, "depth" : 25.4 * mm});
        }
        {
            var Q0;
            Q0=makeQuery(id+"F25.opExtrude","SWEPT_BODY",BODY,{"disambiguationData":[OSD([sQuery(id+"F24.wireOp",EDGE,"E6.bottom"),sQuery(id+"F24.wireOp",EDGE,"E6.top"),sQuery(id+"F24.wireOp",EDGE,"E6.left"),sQuery(id+"F24.wireOp",EDGE,"E6.right")])]});
            transform(context, id + "F61", {"entities" : qUnion([Q0]), "transformType" : TransformType.TRANSLATION_3D, "dx" : 0 * mm, "dy" : 381 * mm, "dz" : 0 * mm, "makeCopy" : true});
        }
        {
            var Q0;
            Q0=makeQuery(id+"F61.opPattern","COPY",FACE,{"derivedFrom":makeQuery(id+"F25.opExtrude","SWEPT_FACE",FACE,{"disambiguationData":[OSD([sQuery(id+"F24.wireOp",EDGE,"E6.top")])]}),"instanceName":"1"});
            var sketch = newSketch(context, id + "F62", { "sketchPlane" : qUnion([Q0])});
            skLineSegment(sketch, "E28", {"start": v(-937.35, 512.75) * mm, "end": v(162.06, 512.75) * mm});
            skLineSegment(sketch, "E29", {"start": v(-937.35, 512.75) * mm, "end": v(-937.35, 0) * mm});
            skSolve(sketch);
        }
        {
            var Q0;
            {var subQ4=sQuery(id+"F62.wireOp",EDGE,"E28");Q0=makeQuery(id+"F62.imprint","IMPRINT",FACE,{"disambiguationData":[TD([[makeQuery(id+"F62.imprint","IMPRINT",EDGE,{"derivedFrom":subQ4}),1.0]])]});}
            extrude(context, id + "F63", {"entities" : qUnion([Q0]), "operationType" : NewBodyOperationType.REMOVE, "oppositeDirection" : true, "depth" : 25.4 * mm});
        }
        {
            var Q0;
            Q0=makeQuery(id+"F61.opPattern","COPY",BODY,{"derivedFrom":makeQuery(id+"F25.opExtrude","SWEPT_BODY",BODY,{"disambiguationData":[OSD([sQuery(id+"F24.wireOp",EDGE,"E6.bottom"),sQuery(id+"F24.wireOp",EDGE,"E6.top"),sQuery(id+"F24.wireOp",EDGE,"E6.left"),sQuery(id+"F24.wireOp",EDGE,"E6.right")])]}),"instanceName":"1"});
            transform(context, id + "F64", {"entities" : qUnion([Q0]), "transformType" : TransformType.TRANSLATION_3D, "dx" : 0 * mm, "dy" : 50.8 * mm, "dz" : 0 * mm, "makeCopy" : true});
        }
        {
            var Q0;
            Q0=makeQuery(id+"F64.opPattern","COPY",FACE,{"derivedFrom":makeQuery(id+"F61.opPattern","COPY",FACE,{"derivedFrom":makeQuery(id+"F25.opExtrude","SWEPT_FACE",FACE,{"disambiguationData":[OSD([sQuery(id+"F24.wireOp",EDGE,"E6.top")])]}),"instanceName":"1"}),"instanceName":"1"});
            var sketch = newSketch(context, id + "F65", { "sketchPlane" : qUnion([Q0])});
            skLineSegment(sketch, "E30", {"start": v(17.6, 512.75) * mm, "end": v(17.6, 0) * mm});
            skSolve(sketch);
        }
        {
            var Q0;
            {var subQ0=sQuery(id+"F65.wireOp",EDGE,"E30");Q0=makeQuery(id+"F65.imprint","IMPRINT",FACE,{"disambiguationData":[TD([[makeQuery(id+"F65.imprint","IMPRINT",EDGE,{"derivedFrom":subQ0}),-1.0]])]});}
            extrude(context, id + "F66", {"entities" : qUnion([Q0]), "operationType" : NewBodyOperationType.REMOVE, "oppositeDirection" : true, "depth" : 25.4 * mm});
        }
    });
